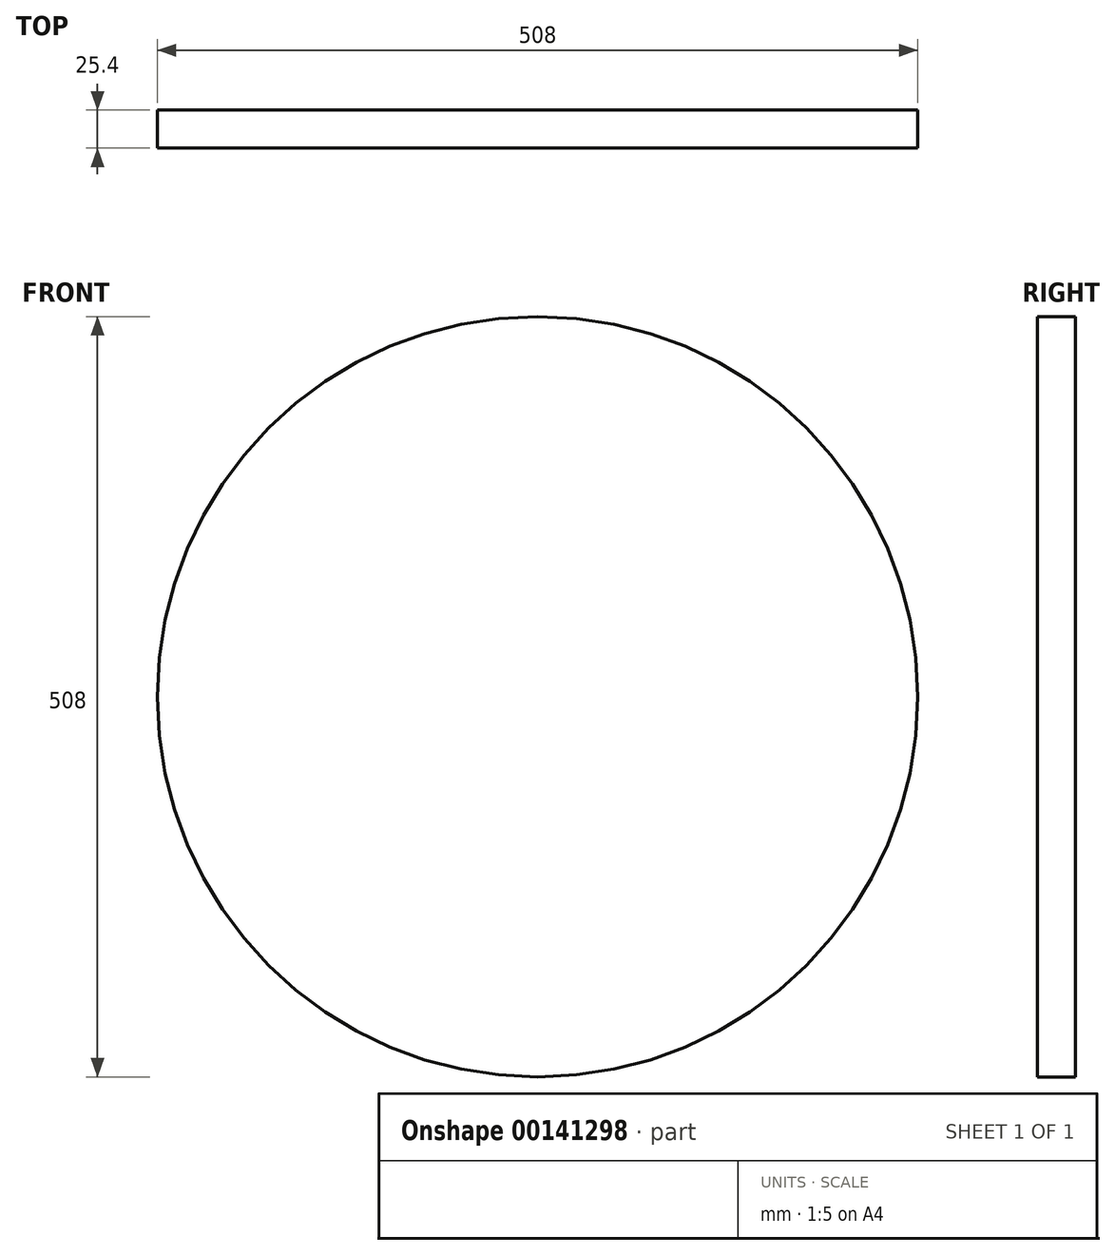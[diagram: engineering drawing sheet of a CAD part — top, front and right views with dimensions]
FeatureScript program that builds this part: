
annotation { "Feature Type Name" : "Feature", "Feature Type Description" : "" }
export const myFeature = defineFeature(function(context is Context, id is Id, definition is map)
    precondition{}
    {
        {
            var Q0;
            Q0=qCreatedBy(makeId("Front.planeOp"),FACE);
            var sketch = newSketch(context, id + "F0", { "sketchPlane" : qUnion([Q0])});
            skCircle(sketch, "E0", {"center": v(-54.57, 46.57) * mm, "radius": 254 * mm});
            skSolve(sketch);
        }
        {
            var Q0;
            Q0=sQuery(id+"F0.wireOp",EDGE,"E0");
            extrude(context, id + "F1", {"bodyType" : ToolBodyType.SURFACE, "surfaceEntities" : qUnion([Q0]), "depth" : 25.4 * mm});
        }
    });
